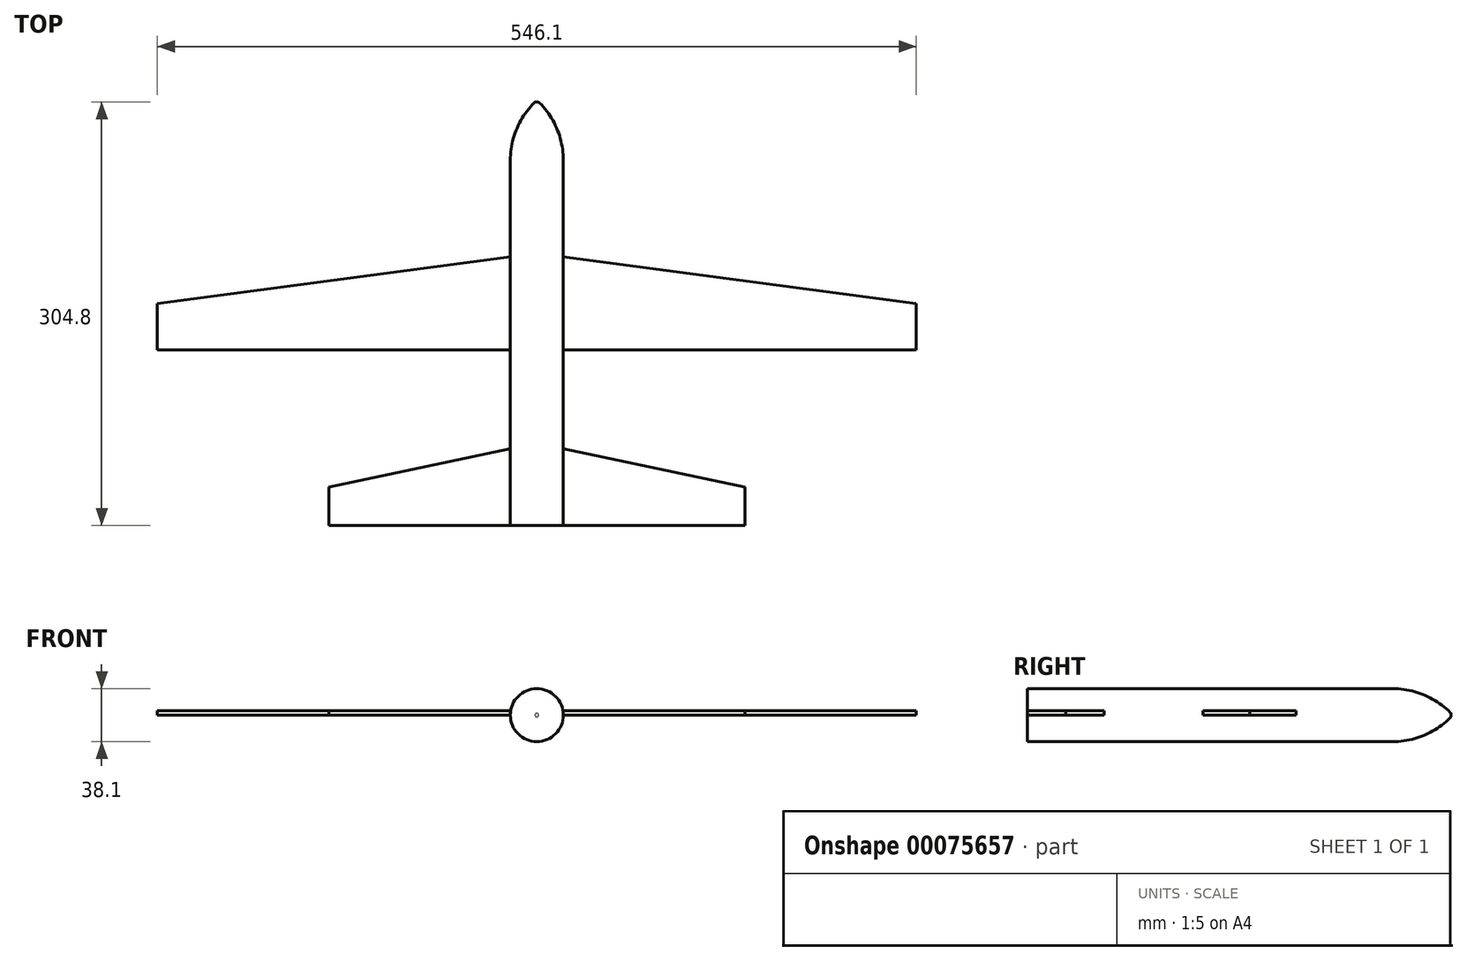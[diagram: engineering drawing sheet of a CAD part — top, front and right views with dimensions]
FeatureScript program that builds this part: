
annotation { "Feature Type Name" : "Feature", "Feature Type Description" : "" }
export const myFeature = defineFeature(function(context is Context, id is Id, definition is map)
    precondition{}
    {
        {
            var Q0;
            Q0=qCreatedBy(makeId("Top.planeOp"),FACE);
            var sketch = newSketch(context, id + "F0", { "sketchPlane" : qUnion([Q0])});
            skLineSegment(sketch, "E0.bottom", {"start": v(0, 0) * mm, "end": v(38.1, 0) * mm});
            skLineSegment(sketch, "E0.top", {"start": v(0, 304.8) * mm, "end": v(38.1, 304.8) * mm});
            skLineSegment(sketch, "E0.left", {"start": v(0, 0) * mm, "end": v(0, 304.8) * mm});
            skLineSegment(sketch, "E0.right", {"start": v(38.1, 0) * mm, "end": v(38.1, 304.8) * mm});
            skLineSegment(sketch, "E1", {"start": v(19.05, 0) * mm, "end": v(19.05, 304.8) * mm});
            skLineSegment(sketch, "E2.MirrorCS", {"start": v(0, 126.41) * mm, "end": v(-254, 126.41) * mm});
            skLineSegment(sketch, "E3.MirrorCS", {"start": v(-254, 159.81) * mm, "end": v(-254, 126.41) * mm});
            skLineSegment(sketch, "E4", {"start": v(-254, 159.81) * mm, "end": v(0, 193.2) * mm});
            skPoint(sketch, "E5.right.start.orphan", {"position": v(292.1, 193.2) * mm});
            skPoint(sketch, "E5.top.end.orphan", {"position": v(292.1, 126.41) * mm});
            skPoint(sketch, "E5.left.end.orphan", {"position": v(38.1, 126.41) * mm});
            skPoint(sketch, "E5.left.start.orphan", {"position": v(38.1, 193.2) * mm});
            skPoint(sketch, "E6.MirrorCS.end.orphan", {"position": v(-254, 193.2) * mm});
            skLineSegment(sketch, "E7.MirrorCS", {"start": v(292.1, 159.81) * mm, "end": v(38.1, 193.2) * mm});
            skLineSegment(sketch, "E8.MirrorCS", {"start": v(38.1, 126.41) * mm, "end": v(292.1, 126.41) * mm});
            skLineSegment(sketch, "E9.MirrorCS", {"start": v(292.1, 159.81) * mm, "end": v(292.1, 126.41) * mm});
            skLineSegment(sketch, "E10.bottom", {"start": v(38.1, 0) * mm, "end": v(168.8, 0) * mm});
            skLineSegment(sketch, "E10.left", {"start": v(38.1, 0) * mm, "end": v(38.1, 55.21) * mm});
            skLineSegment(sketch, "E10.right", {"start": v(168.8, 0) * mm, "end": v(168.8, 27.6) * mm});
            skLineSegment(sketch, "E11.MirrorCS", {"start": v(-130.7, 0) * mm, "end": v(-130.7, 27.6) * mm});
            skLineSegment(sketch, "E12.MirrorCS", {"start": v(0, 0) * mm, "end": v(-130.7, 0) * mm});
            skLineSegment(sketch, "E13", {"start": v(-130.7, 27.6) * mm, "end": v(0, 55.21) * mm});
            skLineSegment(sketch, "E14", {"start": v(168.8, 27.6) * mm, "end": v(38.1, 55.21) * mm});
            skPoint(sketch, "E15.orphan", {"position": v(168.8, 55.21) * mm});
            skPoint(sketch, "E16.MirrorCS.end.orphan", {"position": v(-130.7, 55.21) * mm});
            skSolve(sketch);
        }
        {
            var Q0;
            {var subQ0=sQuery(id+"F0.wireOp",EDGE,"E0.left");Q0=makeQuery(id+"F0.imprint","IMPRINT",FACE,{"disambiguationData":[TD([[makeQuery(id+"F0.imprint","IMPRINT",EDGE,{"derivedFrom":subQ0}),-1.0]])]});}
            var Q1;
            Q1=sQuery(id+"F0.wireOp",EDGE,"E1");
            revolve(context, id + "F1", {"entities" : qUnion([Q0]), "axis" : qUnion([Q1]), "revolveType" : RevolveType.FULL});
        }
        {
            var Q0;
            {var subQ0=sQuery(id+"F0.wireOp",EDGE,"E2.MirrorCS");Q0=makeQuery(id+"F0.imprint","IMPRINT",FACE,{"disambiguationData":[TD([[makeQuery(id+"F0.imprint","IMPRINT",EDGE,{"derivedFrom":subQ0}),-1.0]])]});}
            var Q1;
            {var subQ0=sQuery(id+"F0.wireOp",EDGE,"E7.MirrorCS");Q1=makeQuery(id+"F0.imprint","IMPRINT",FACE,{"disambiguationData":[TD([[makeQuery(id+"F0.imprint","IMPRINT",EDGE,{"derivedFrom":subQ0}),1.0]])]});}
            var Q2;
            Q2=makeQuery(id+"F0.imprint","IMPRINT",FACE,{"disambiguationData":[TD([[makeQuery(id+"F0.imprint","IMPRINT",EDGE,{"derivedFrom":sQuery(id+"F0.wireOp",EDGE,"E11.MirrorCS")}),-1.0]])]});
            var Q3;
            Q3=makeQuery(id+"F0.imprint","IMPRINT",FACE,{"disambiguationData":[TD([[makeQuery(id+"F0.imprint","IMPRINT",EDGE,{"derivedFrom":sQuery(id+"F0.wireOp",EDGE,"E10.bottom")}),1.0]])]});
            extrude(context, id + "F2", {"entities" : qUnion([Q0, Q1, Q2, Q3]), "operationType" : NewBodyOperationType.ADD, "depth" : 3.17 * mm});
        }
        {
            var Q0;
            Q0=makeQuery(id+"F1.opRevolve","SWEPT_EDGE",EDGE,{"disambiguationData":[OSD([sQuery(id+"F0.wireOp",EDGE,"E0.top"),sQuery(id+"F0.wireOp",EDGE,"E0.left")])]});
            chamfer(context, id + "F3", {"entities" : qUnion([Q0]), "width" : 17.78 * mm, "tangentPropagation" : true});
        }
        {
            var Q0;
            {var subQ0=sQuery(id+"F0.wireOp",EDGE,"E0.left");Q0=makeQuery(id+"F3.opChamfer","BLEND_EDGE",EDGE,{"blendedFrom":[makeQuery(id+"F1.opRevolve","SWEPT_EDGE",EDGE,{"disambiguationData":[OSD([sQuery(id+"F0.wireOp",EDGE,"E0.top"),subQ0])]}),makeQuery(id+"F1.opRevolve","SWEPT_FACE",FACE,{"disambiguationData":[OSD([subQ0])]})],"blendedInto":[makeQuery(id+"F1.opRevolve","SWEPT_FACE",FACE,{"disambiguationData":[OSD([subQ0])]})]});}
            fillet(context, id + "F4", {"entities" : qUnion([Q0]), "radius" : 58.42 * mm, "tangentPropagation" : true, "allowEdgeOverflow" : false});
        }
    });
